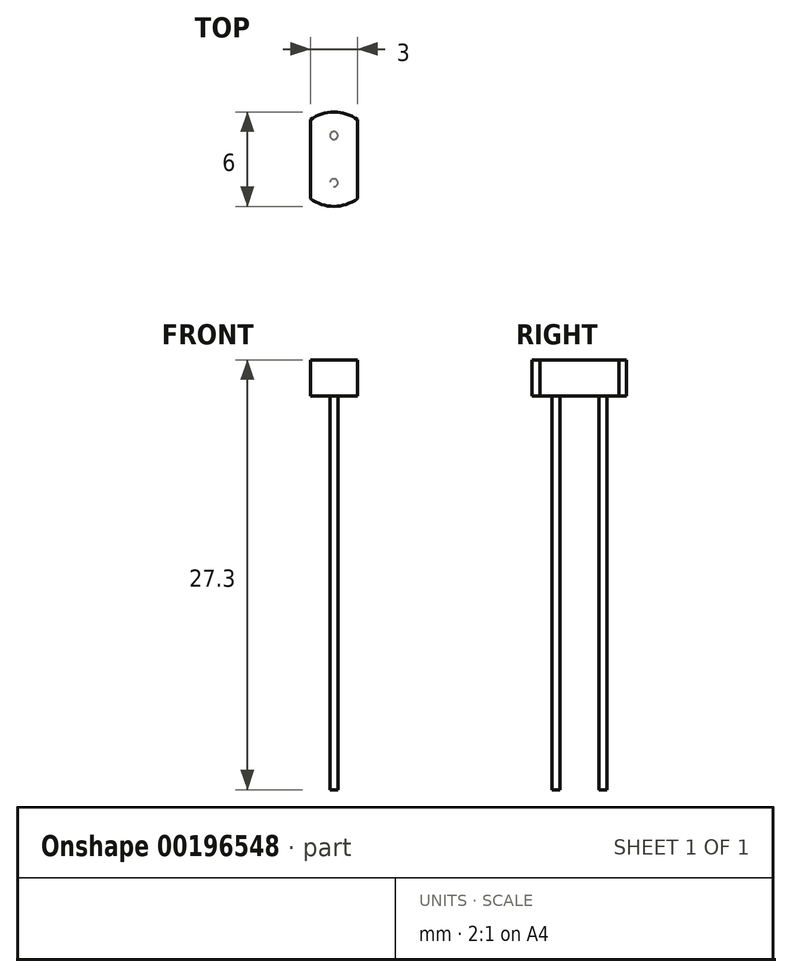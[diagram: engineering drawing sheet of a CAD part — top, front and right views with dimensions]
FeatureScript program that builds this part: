
annotation { "Feature Type Name" : "Feature", "Feature Type Description" : "" }
export const myFeature = defineFeature(function(context is Context, id is Id, definition is map)
    precondition{}
    {
        {
            var Q0;
            Q0=qCreatedBy(makeId("Top.planeOp"),FACE);
            var sketch = newSketch(context, id + "F0", { "sketchPlane" : qUnion([Q0])});
            skLineSegment(sketch, "E0", {"start": v(0, 2.5) * mm, "end": v(0, -2.5) * mm});
            skLineSegment(sketch, "E1", {"start": v(3, 2.5) * mm, "end": v(3, -2.5) * mm});
            skArc(sketch, "E2", {"start": v(3, 2.5) * mm, "mid": v(1.5, 3) * mm, "end": v(0, 2.5) * mm});
            skArc(sketch, "E3", {"start": v(0, -2.5) * mm, "mid": v(1.5, -3) * mm, "end": v(3, -2.5) * mm});
            skSolve(sketch);
        }
        {
            var Q0;
            Q0 = qSketchRegion(id + "F0", true);
            extrude(context, id + "F1", {"entities" : qUnion([Q0]), "depth" : 2.3 * mm});
        }
        {
            var Q0;
            Q0=makeQuery(id+"F1.opExtrude","CAP_FACE",FACE,{"disambiguationData":[OSD([sQuery(id+"F0.wireOp",EDGE,"E0"),sQuery(id+"F0.wireOp",EDGE,"E1"),sQuery(id+"F0.wireOp",EDGE,"E2"),sQuery(id+"F0.wireOp",EDGE,"E3")])],"isStart":true});
            var sketch = newSketch(context, id + "F2", { "sketchPlane" : qUnion([Q0])});
            skCircle(sketch, "E4", {"center": v(1.5, 1.5) * mm, "radius": 0.25 * mm});
            skCircle(sketch, "E5", {"center": v(1.5, -1.5) * mm, "radius": 0.25 * mm});
            skSolve(sketch);
        }
        {
            var Q0;
            Q0 = qSketchRegion(id + "F2", true);
            extrude(context, id + "F3", {"entities" : qUnion([Q0]), "operationType" : NewBodyOperationType.ADD, "depth" : 25 * mm});
        }
    });
